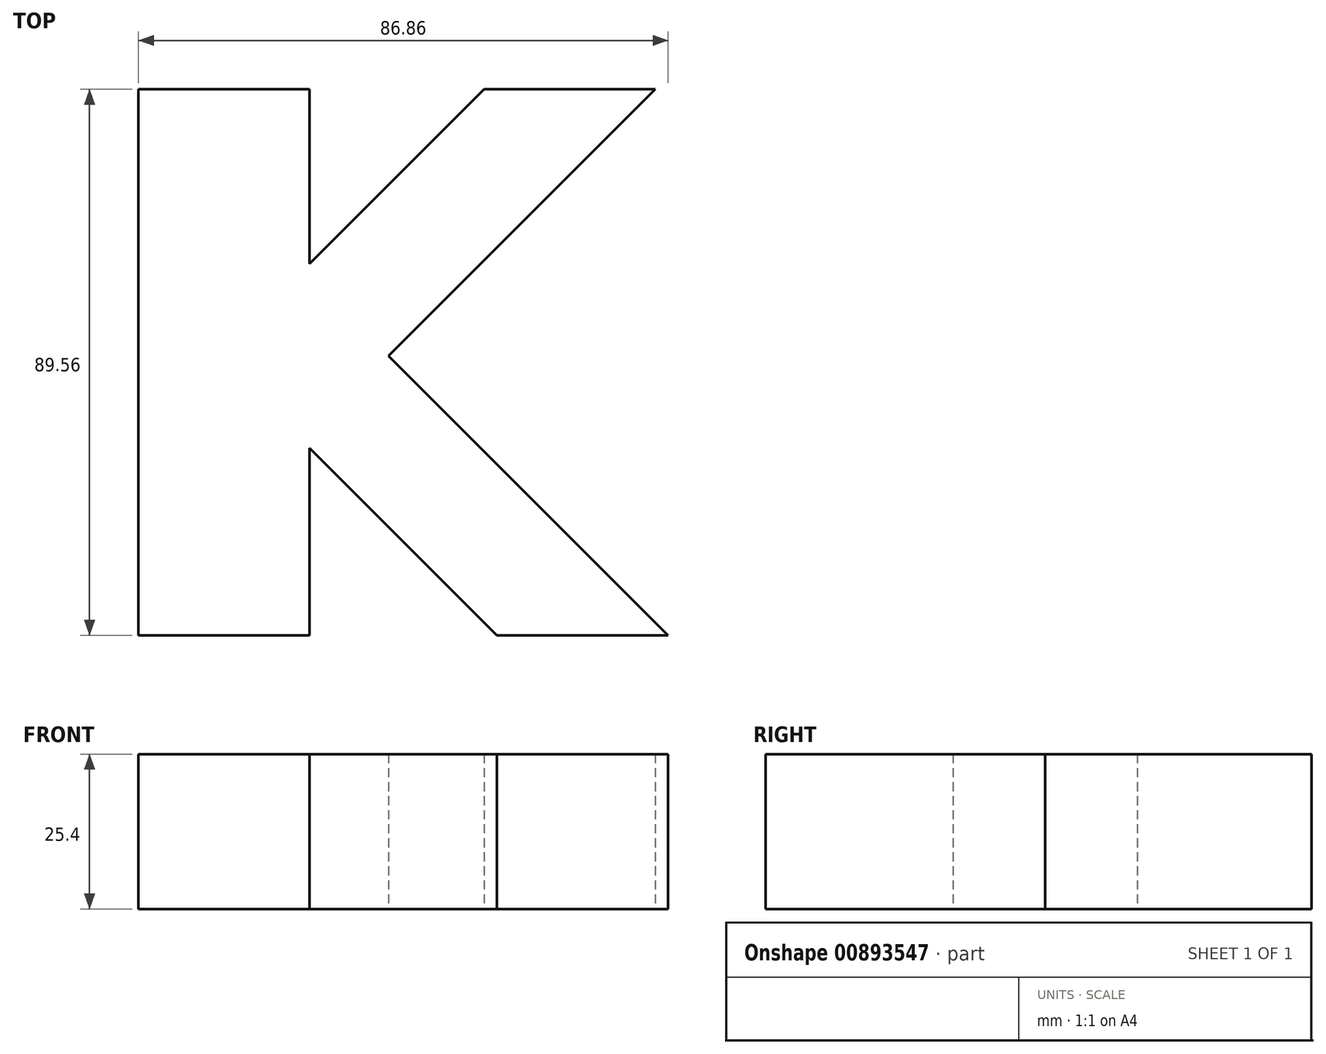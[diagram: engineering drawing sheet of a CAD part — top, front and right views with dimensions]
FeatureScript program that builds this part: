
annotation { "Feature Type Name" : "Feature", "Feature Type Description" : "" }
export const myFeature = defineFeature(function(context is Context, id is Id, definition is map)
    precondition{}
    {
        {
            var Q0;
            Q0=qCreatedBy(makeId("Top.planeOp"),FACE);
            var sketch = newSketch(context, id + "F0", { "sketchPlane" : qUnion([Q0])});
            skLineSegment(sketch, "E0", {"start": v(-37.5, -48.8) * mm, "end": v(-37.5, 40.75) * mm});
            skLineSegment(sketch, "E1", {"start": v(-37.5, 40.75) * mm, "end": v(-9.44, 40.75) * mm});
            skLineSegment(sketch, "E2", {"start": v(-9.44, 40.75) * mm, "end": v(-9.44, 12.14) * mm});
            skLineSegment(sketch, "E3", {"start": v(-9.44, 12.14) * mm, "end": v(19.16, 40.75) * mm});
            skLineSegment(sketch, "E4", {"start": v(19.16, 40.75) * mm, "end": v(47.22, 40.75) * mm});
            skLineSegment(sketch, "E5", {"start": v(47.22, 40.75) * mm, "end": v(3.5, -2.97) * mm});
            skLineSegment(sketch, "E6", {"start": v(3.5, -2.97) * mm, "end": v(49.35, -48.8) * mm});
            skLineSegment(sketch, "E7", {"start": v(49.35, -48.8) * mm, "end": v(21.29, -48.8) * mm});
            skLineSegment(sketch, "E8", {"start": v(21.29, -48.8) * mm, "end": v(-9.44, -18.08) * mm});
            skLineSegment(sketch, "E9", {"start": v(-9.44, -18.08) * mm, "end": v(-9.44, -48.8) * mm});
            skLineSegment(sketch, "E10", {"start": v(-9.44, -48.8) * mm, "end": v(-37.5, -48.8) * mm});
            skSolve(sketch);
        }
        {
            var Q0;
            Q0=makeQuery(id+"F0.imprint","IMPRINT",FACE,{"disambiguationData":[TD([[makeQuery(id+"F0.imprint","IMPRINT",EDGE,{"derivedFrom":sQuery(id+"F0.wireOp",EDGE,"E0")}),-1.0]])]});
            extrude(context, id + "F1", {"entities" : qUnion([Q0]), "depth" : 25.4 * mm, "offsetDistance" : 25.4 * mm});
        }
    });
